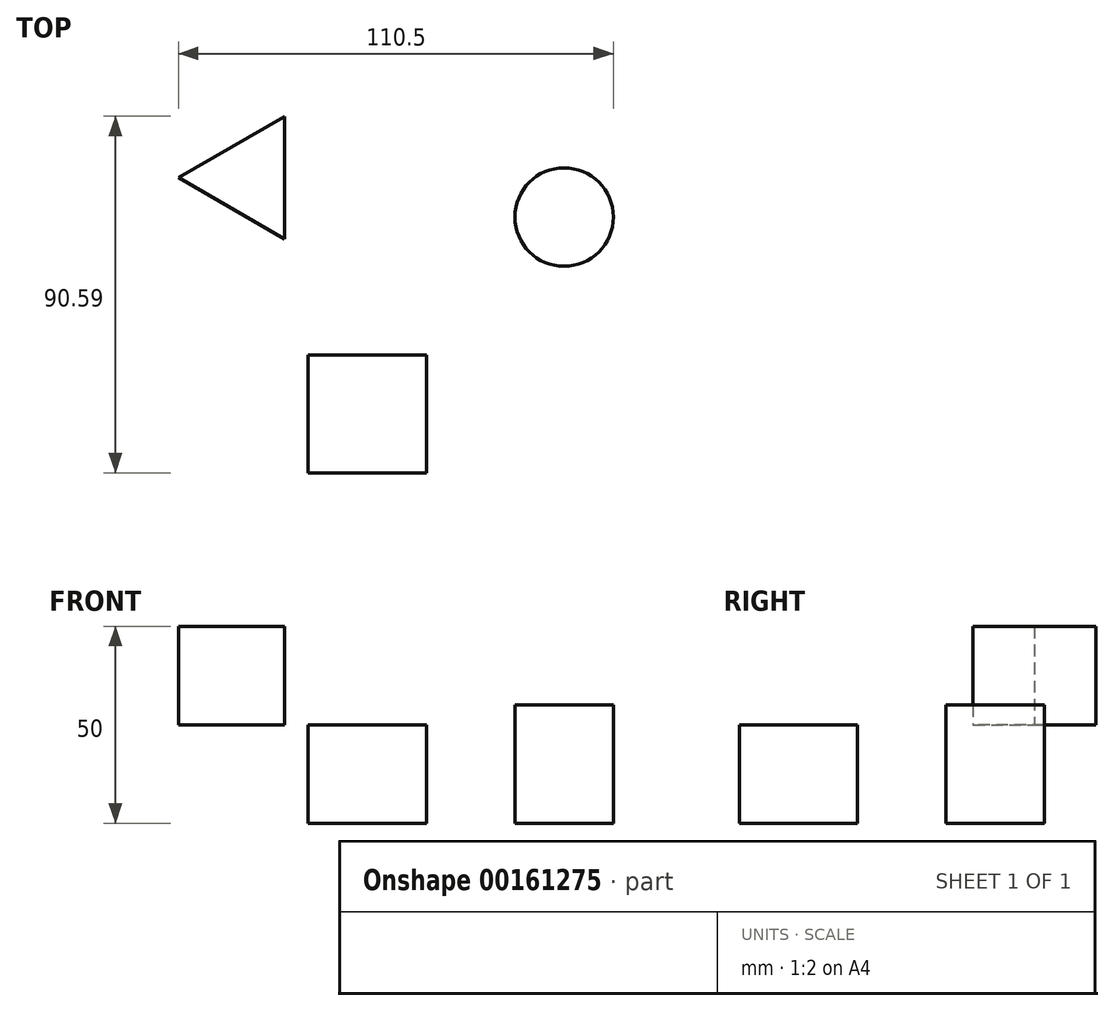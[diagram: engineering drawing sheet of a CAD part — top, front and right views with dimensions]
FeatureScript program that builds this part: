
annotation { "Feature Type Name" : "Feature", "Feature Type Description" : "" }
export const myFeature = defineFeature(function(context is Context, id is Id, definition is map)
    precondition{}
    {
        {
            var Q0;
            Q0=qCreatedBy(makeId("Top.planeOp"),FACE);
            var sketch = newSketch(context, id + "F0", { "sketchPlane" : qUnion([Q0])});
            skLineSegment(sketch, "E0.bottom", {"start": v(-15, -15) * mm, "end": v(15, -15) * mm});
            skLineSegment(sketch, "E0.top", {"start": v(-15, 15) * mm, "end": v(15, 15) * mm});
            skLineSegment(sketch, "E0.left", {"start": v(-15, -15) * mm, "end": v(-15, 15) * mm});
            skLineSegment(sketch, "E0.right", {"start": v(15, -15) * mm, "end": v(15, 15) * mm});
            skPoint(sketch, "E0.middle", {"position": v(0, 0) * mm});
            skCircle(sketch, "E1", {"center": v(50, 50) * mm, "radius": 12.5 * mm});
            skSolve(sketch);
        }
        {
            var Q0;
            Q0=makeQuery(id+"F0.imprint","IMPRINT",FACE,{"disambiguationData":[TD([[makeQuery(id+"F0.imprint","IMPRINT",EDGE,{"derivedFrom":sQuery(id+"F0.wireOp",EDGE,"E0.bottom")}),1.0]])]});
            extrude(context, id + "F1", {"entities" : qUnion([Q0]), "depth" : 25 * mm});
        }
        {
            var Q0;
            Q0=makeQuery(id+"F0.imprint","IMPRINT",FACE,{"disambiguationData":[TD([[makeQuery(id+"F0.imprint","IMPRINT",EDGE,{"derivedFrom":sQuery(id+"F0.wireOp",EDGE,"E1")}),1.0]])]});
            extrude(context, id + "F2", {"entities" : qUnion([Q0]), "depth" : 30 * mm});
        }
        {
            var Q0;
            Q0=qCreatedBy(makeId("Top.planeOp"),FACE);
            cPlane(context, id + "F3", {"entities" : qUnion([Q0]), "cplaneType" : CPlaneType.OFFSET, "offset" : 25 * mm, "width" : 150 * mm, "height" : 150 * mm});
        }
        {
            var Q0;
            Q0=qCreatedBy(id+"F3.planeOp",FACE);
            var sketch = newSketch(context, id + "F4", { "sketchPlane" : qUnion([Q0])});
            skCircle(sketch, "E2.cCircle", {"center": v(-30, 60) * mm, "radius": 9 * mm, "construction": true});
            skLineSegment(sketch, "E2.0", {"start": v(-21, 44.41) * mm, "end": v(-48, 60) * mm});
            skLineSegment(sketch, "E2.1", {"start": v(-48, 60) * mm, "end": v(-21, 75.59) * mm});
            skLineSegment(sketch, "E2.2", {"start": v(-21, 75.59) * mm, "end": v(-21, 44.41) * mm});
            skPoint(sketch, "E2.0.midPoint", {"position": v(-34.5, 52.2) * mm});
            skLineSegment(sketch, "E3", {"start": v(-30, 60) * mm, "end": v(-21, 75.59) * mm, "construction": true});
            skLineSegment(sketch, "E4", {"start": v(-30, 60) * mm, "end": v(-7.78, 60) * mm, "construction": true});
            skSolve(sketch);
        }
        {
            var Q0;
            Q0=makeQuery(id+"F4.imprint","IMPRINT",FACE,{"disambiguationData":[TD([[makeQuery(id+"F4.imprint","IMPRINT",EDGE,{"derivedFrom":sQuery(id+"F4.wireOp",EDGE,"E2.0")}),-1.0]])]});
            extrude(context, id + "F5", {"entities" : qUnion([Q0]), "depth" : 25 * mm});
        }
    });
